# Revit family: triona_round_a_312392_002_2_730_778a
name_source: partatom
category: Lighting Fixtures
units: mm (PartAtom-declared; Revit-internal decimal feet)

## family parameters
Cut with Voids When Loaded = No
Host = Face
Light Source = No
Part Type = Normal
Room Calculation Point = No
Round Connector Dimension = Use Diameter
Shared = No

## types (1)
- TuneableWhite 846 (1 x LED Modul 846, 7400 lm, 4600)
    Apparent Load = 85 VA
    CIE Flux Codes = 50 80 96 73 100
    Color Rendering = 80
    Color Temperature = 4600
    Default Elevation = 1800 mm
    Description = Series: TRIONA round
Decorative round LED surface-mounted luminaire. Flat, seamless frame: aluminium extrusion profile, powder coated. Cover made of sheet steel, powder-coated. Direct light emission through a diffuser plastic opal. Indirect light emission through a flush diffuser made of satin-finish plastic. Lightguide and diffuser made of non-yellowing plastic (PMMA). Lateral light emission (RZB SIDELITE technology) for above-average homogeneous light distribution. Direct 70%, indirect 30% light emission. Tunable white versions, dynamically adjustable from 2700 K to 6500 K. Suitable for Ceiling mounting, Wall (surface). Tool-free mounting via bayonet connection. Electronic ballast included. Very easy installation thanks to Plug+Play connection. With Casambi smart+free Bluetooth control for wireless network and operation using Android / iOS devices, free app available for download. Ideal for use as part of the Human Centric Lighting concept in connection with RZB light management systems. 
Colour: traffic white, matt (RAL 9016)
Diameter: 1009 mm
Height: 88 mm
Lamp: LED
Socket: without socket
Colour temperature: 2700K - 6500K
Colour rendering index (CRI): 80
System power: 85 W
Rated luminous flux: 7400 lm
Luminous efficiency: 87 lm/W
System power 2: 88 W
Rated luminous flux 2: 7050 lm
Luminous efficiency 2: 80 lm/W
System power 3: 87 W
Rated luminous flux 3: 7100 lm
Luminous efficiency 3: 82 lm/W
Control gear: Dimmable Bluetooth converter
Protection class: I
Type of protection: IP 20
    Height = 88 mm
    Lamp = 1 x LED Modul 846
    Lamp Light Flux = 7400 lm
    Lamp count = 1
    Length = 1009 mm
    Lifetime = 50000 h
    Luminous efficacy = 87 lm/W
    Manufacturer = RZB
    ModVariant = No
    Model = 312392.002.2.730
    Mounting Place = Ceiling
    Mounting Type = Surface mounted
    Number of Poles = 1
    OnlyDefault = Yes
    Power Factor = 1
    Product Name = TRIONA round A
    Product group = Surface mounted modular luminaires
    ProductGroupID = 306
    Protection Class = Protection class I
    Protection Degree = IP 20
    RLX_Detail_Level = 1
    RLX_Emergency_Light_Flux = 0 lm
    RLX_Emergency_Type = 0
    RLX_Emergency_Type_DB = No
    RlxData = <blob elided: 44997 chars, md5=4bd1c0b7>
    Socket = socket
    Standby Power = 0 W
    System Light Flux = 7400 lm
    System Power = 85 W
    Type Comments = TuneableWhite 846
    Type Image = 312392.002.jpg
    URL = http://relux.com
    VarID = tuneablewhite_846
    Voltage = 230 V
    Voltage Range = 220-240 V
    Weight = 0.00 kg
    Width = 0 mm  [stored 0 ft]

note: [stored X ft] marks values corroborated as IEEE doubles in the binary element streams (Revit-internal decimal feet)

## geometry (parser evidence)
native form markers: Sweep x13
no freeform markers — native parametric forms only
